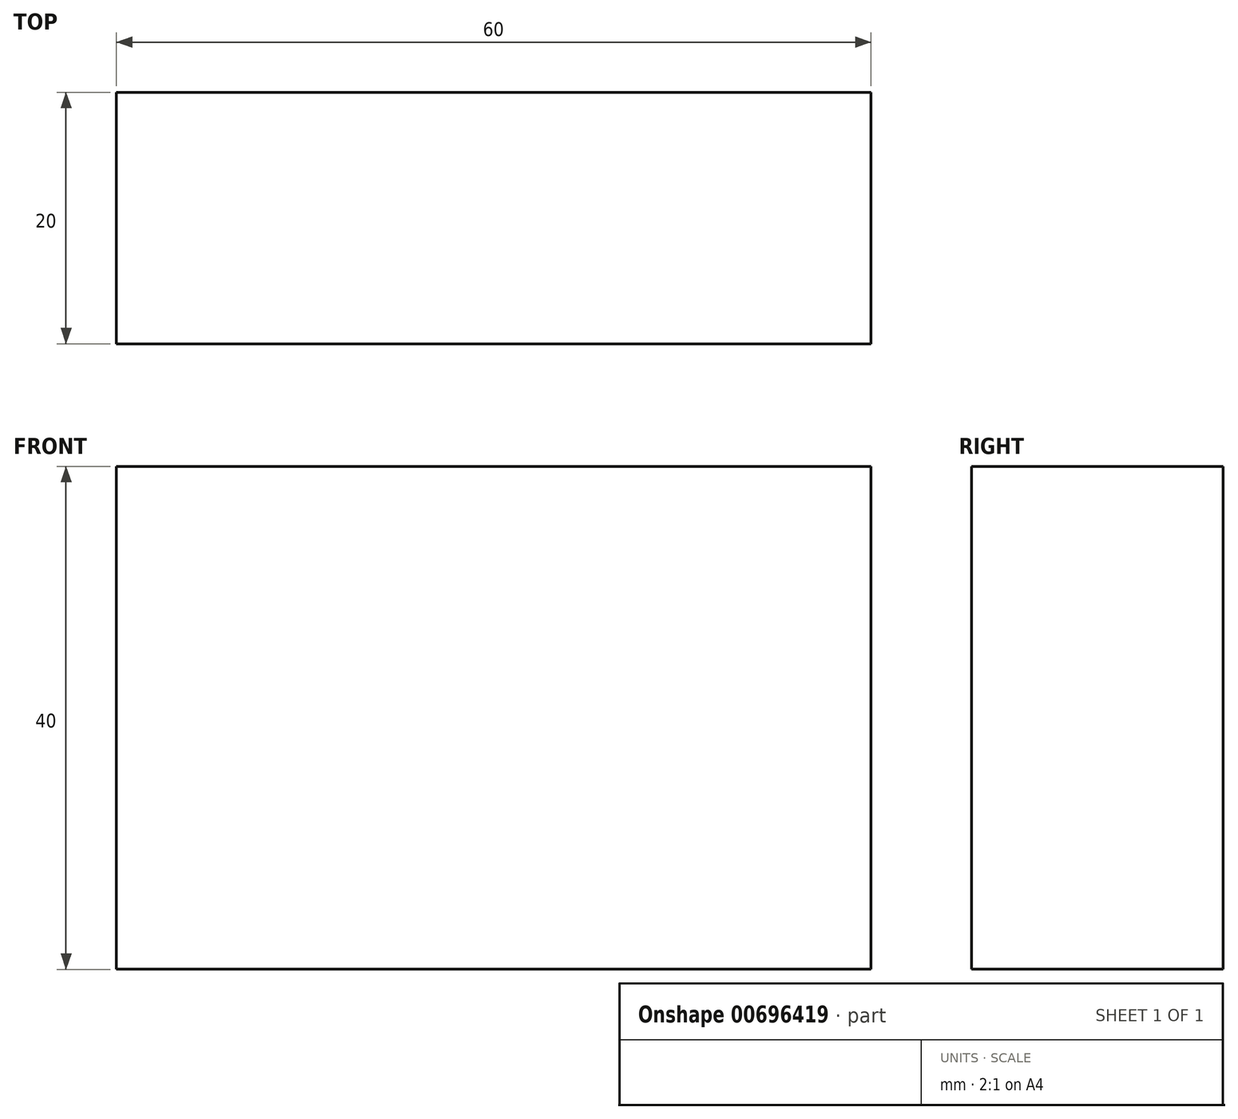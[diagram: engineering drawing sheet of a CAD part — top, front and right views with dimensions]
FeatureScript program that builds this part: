
annotation { "Feature Type Name" : "Feature", "Feature Type Description" : "" }
export const myFeature = defineFeature(function(context is Context, id is Id, definition is map)
    precondition{}
    {
        {
            var Q0;
            Q0=qCreatedBy(makeId("Front.planeOp"),FACE);
            var sketch = newSketch(context, id + "F0", { "sketchPlane" : qUnion([Q0])});
            skLineSegment(sketch, "E0", {"start": v(-31.5, 23.06) * mm, "end": v(28.5, 23.06) * mm});
            skLineSegment(sketch, "E1", {"start": v(28.5, 23.06) * mm, "end": v(28.5, -16.94) * mm});
            skLineSegment(sketch, "E2", {"start": v(28.5, -16.94) * mm, "end": v(-31.5, -16.94) * mm});
            skLineSegment(sketch, "E3", {"start": v(-31.5, -16.94) * mm, "end": v(-31.5, 23.06) * mm});
            skSolve(sketch);
        }
        {
            var Q0;
            Q0 = qSketchRegion(id + "F0", true);
            extrude(context, id + "F1", {"entities" : qUnion([Q0]), "depth" : 20 * mm, "offsetDistance" : 25 * mm});
        }
    });
